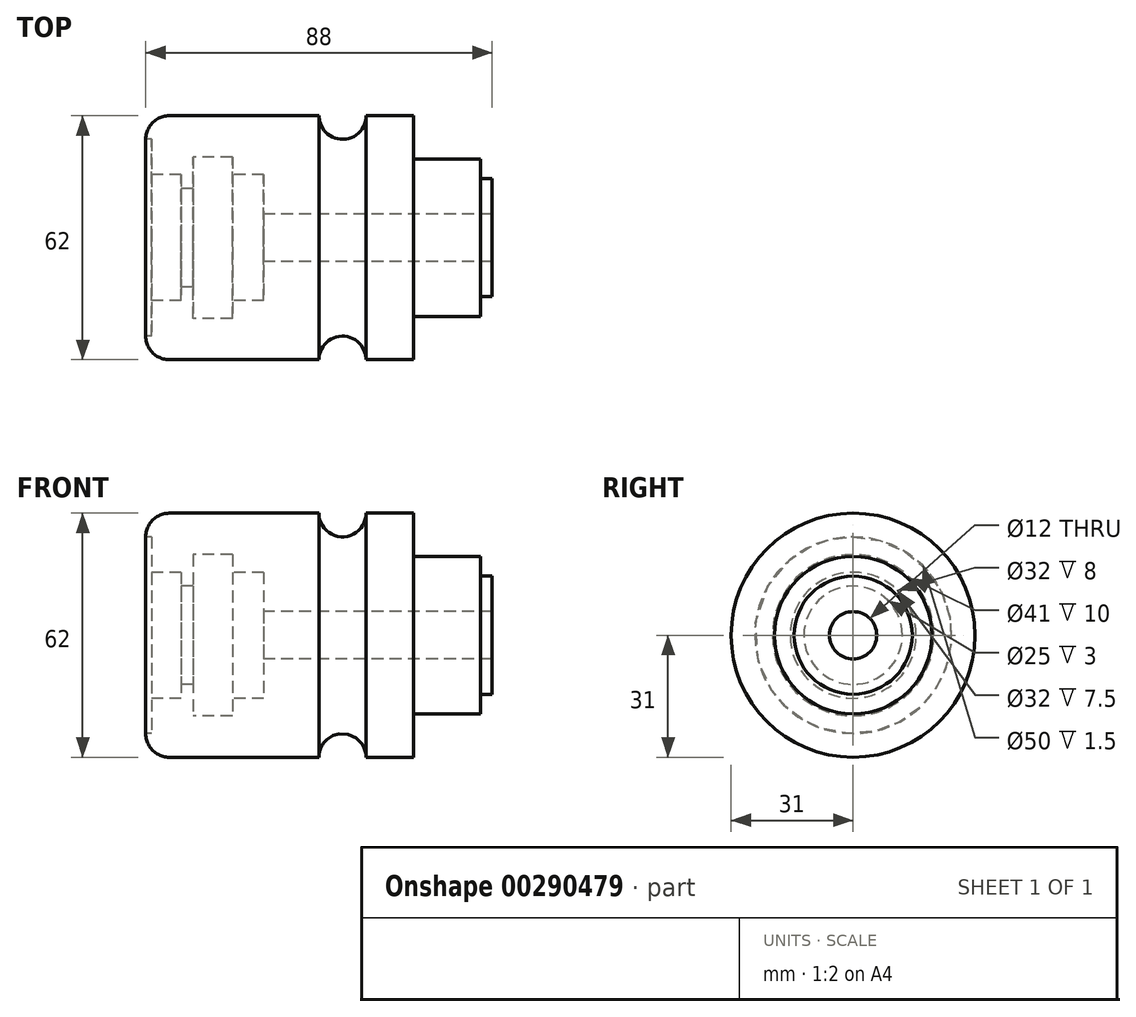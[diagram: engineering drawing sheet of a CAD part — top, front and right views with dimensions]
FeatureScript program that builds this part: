
annotation { "Feature Type Name" : "Feature", "Feature Type Description" : "" }
export const myFeature = defineFeature(function(context is Context, id is Id, definition is map)
    precondition{}
    {
        {
            var Q0;
            Q0=qCreatedBy(makeId("Front.planeOp"),FACE);
            var sketch = newSketch(context, id + "F0", { "sketchPlane" : qUnion([Q0])});
            skLineSegment(sketch, "E0", {"start": v(0, 0) * mm, "end": v(126.7, 0) * mm, "construction": true});
            skLineSegment(sketch, "E1", {"start": v(0, 0) * mm, "end": v(0, 31) * mm});
            skLineSegment(sketch, "E2", {"start": v(0, 31) * mm, "end": v(44, 31) * mm});
            skLineSegment(sketch, "E3", {"start": v(68, 31) * mm, "end": v(68, 20) * mm});
            skLineSegment(sketch, "E4", {"start": v(68, 20) * mm, "end": v(85, 20) * mm});
            skLineSegment(sketch, "E5", {"start": v(85, 20) * mm, "end": v(85, 15) * mm});
            skLineSegment(sketch, "E6", {"start": v(85, 15) * mm, "end": v(88, 15) * mm});
            skLineSegment(sketch, "E7", {"start": v(88, 15) * mm, "end": v(88, 0) * mm});
            skLineSegment(sketch, "E8", {"start": v(88, 0) * mm, "end": v(0, 0) * mm});
            skArc(sketch, "E9", {"start": v(44, 31) * mm, "mid": v(50, 25) * mm, "end": v(56, 31) * mm});
            skLineSegment(sketch, "E10.trimOffspring", {"start": v(56, 31) * mm, "end": v(68, 31) * mm});
            skSolve(sketch);
        }
        {
            var Q0;
            Q0 = qSketchRegion(id + "F0", true);
            var Q1;
            Q1=sQuery(id+"F0.wireOp",EDGE,"E0");
            revolve(context, id + "F1", {"entities" : qUnion([Q0]), "axis" : qUnion([Q1]), "revolveType" : RevolveType.FULL});
        }
        {
            var Q0;
            Q0=qCreatedBy(makeId("Front.planeOp"),FACE);
            var sketch = newSketch(context, id + "F2", { "sketchPlane" : qUnion([Q0])});
            skLineSegment(sketch, "E11", {"start": v(0, 0) * mm, "end": v(-21.62, 0) * mm, "construction": true});
            skLineSegment(sketch, "E12", {"start": v(0, 0) * mm, "end": v(0, 25) * mm});
            skLineSegment(sketch, "E13", {"start": v(0, 25) * mm, "end": v(1.5, 25) * mm});
            skLineSegment(sketch, "E14", {"start": v(1.5, 25) * mm, "end": v(1.5, 16) * mm});
            skLineSegment(sketch, "E15", {"start": v(1.5, 16) * mm, "end": v(9, 16) * mm});
            skLineSegment(sketch, "E16", {"start": v(9, 16) * mm, "end": v(9, 12.5) * mm});
            skLineSegment(sketch, "E17", {"start": v(9, 12.5) * mm, "end": v(12, 12.5) * mm});
            skLineSegment(sketch, "E18", {"start": v(12, 12.5) * mm, "end": v(12, 20.5) * mm});
            skLineSegment(sketch, "E19", {"start": v(12, 20.5) * mm, "end": v(22, 20.5) * mm});
            skLineSegment(sketch, "E20", {"start": v(22, 20.5) * mm, "end": v(22, 16) * mm});
            skLineSegment(sketch, "E21", {"start": v(22, 16) * mm, "end": v(30, 16) * mm});
            skLineSegment(sketch, "E22", {"start": v(30, 16) * mm, "end": v(30, 6) * mm});
            skLineSegment(sketch, "E23", {"start": v(30, 6) * mm, "end": v(88, 6) * mm});
            skLineSegment(sketch, "E24", {"start": v(88, 6) * mm, "end": v(88, 0) * mm});
            skLineSegment(sketch, "E25", {"start": v(88, 0) * mm, "end": v(0, 0) * mm});
            skSolve(sketch);
        }
        {
            var Q0;
            Q0 = qSketchRegion(id + "F2", true);
            var Q1;
            Q1=sQuery(id+"F2.wireOp",EDGE,"E11");
            revolve(context, id + "F3", {"operationType" : NewBodyOperationType.REMOVE, "entities" : qUnion([Q0]), "axis" : qUnion([Q1]), "revolveType" : RevolveType.FULL, "oppositeDirection" : true});
        }
        {
            var Q0;
            Q0=makeQuery(id+"F1.opRevolve","SWEPT_EDGE",EDGE,{"disambiguationData":[OSD([sQuery(id+"F0.wireOp",EDGE,"E1"),sQuery(id+"F0.wireOp",EDGE,"E2")])]});
            fillet(context, id + "F4", {"entities" : qUnion([Q0]), "radius" : 6 * mm, "tangentPropagation" : true, "allowEdgeOverflow" : false});
        }
    });
